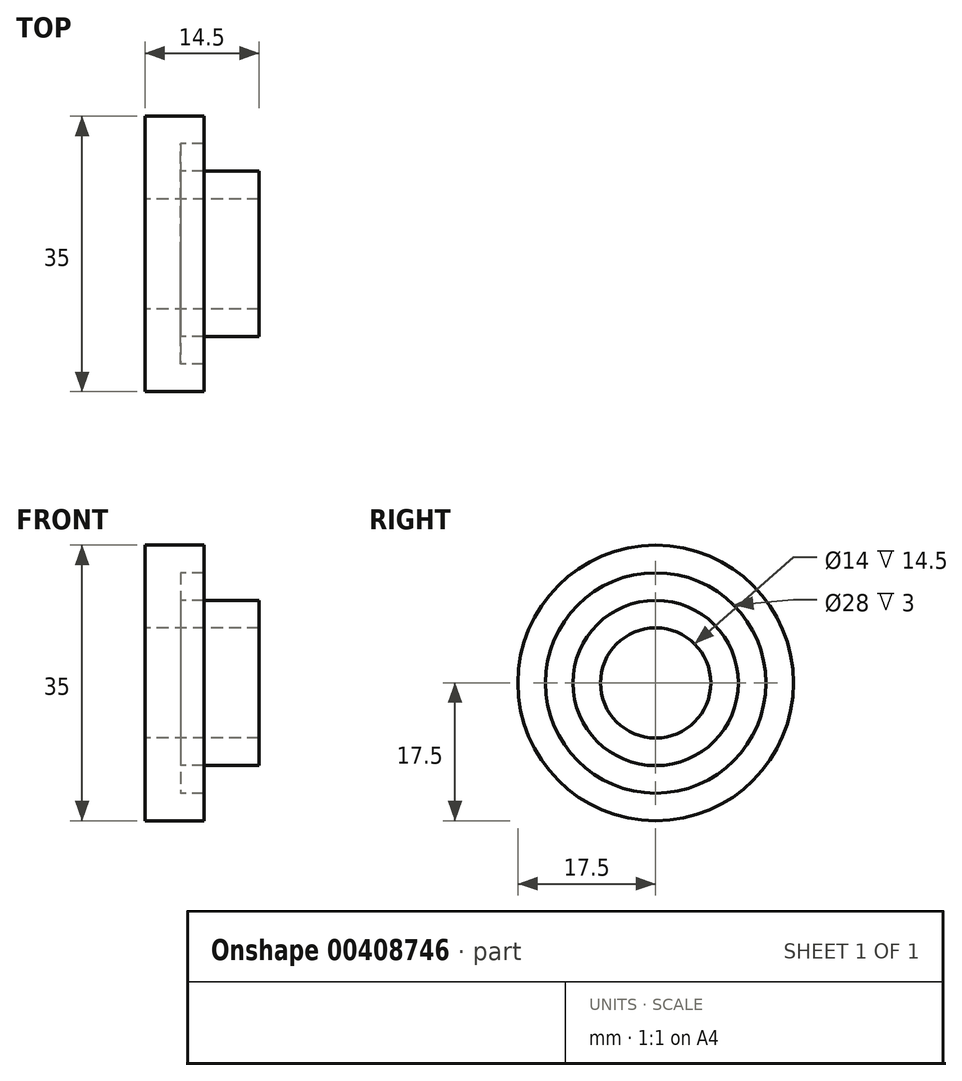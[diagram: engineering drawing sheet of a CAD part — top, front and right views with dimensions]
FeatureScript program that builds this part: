
annotation { "Feature Type Name" : "Feature", "Feature Type Description" : "" }
export const myFeature = defineFeature(function(context is Context, id is Id, definition is map)
    precondition{}
    {
        {
            var Q0;
            Q0=qCreatedBy(makeId("Front.planeOp"),FACE);
            var sketch = newSketch(context, id + "F0", { "sketchPlane" : qUnion([Q0])});
            skLineSegment(sketch, "E0", {"start": v(14.5, 7) * mm, "end": v(0, 7) * mm});
            skLineSegment(sketch, "E1", {"start": v(0, 7) * mm, "end": v(0, 17.5) * mm});
            skLineSegment(sketch, "E2", {"start": v(0, 17.5) * mm, "end": v(7.5, 17.5) * mm});
            skLineSegment(sketch, "E3", {"start": v(7.5, 17.5) * mm, "end": v(7.5, 14) * mm});
            skLineSegment(sketch, "E4", {"start": v(7.5, 14) * mm, "end": v(4.5, 14) * mm});
            skLineSegment(sketch, "E5", {"start": v(4.5, 14) * mm, "end": v(4.5, 10.5) * mm});
            skLineSegment(sketch, "E6", {"start": v(4.5, 10.5) * mm, "end": v(14.5, 10.5) * mm});
            skLineSegment(sketch, "E7", {"start": v(14.5, 10.5) * mm, "end": v(14.5, 7) * mm});
            skLineSegment(sketch, "E8", {"start": v(0, 0) * mm, "end": v(45.5, 0) * mm, "construction": true});
            skSolve(sketch);
        }
        {
            var Q0;
            Q0=makeQuery(id+"F0.imprint","IMPRINT",FACE,{"disambiguationData":[TD([[makeQuery(id+"F0.imprint","IMPRINT",EDGE,{"derivedFrom":sQuery(id+"F0.wireOp",EDGE,"E0")}),-1.0]])]});
            var Q1;
            Q1=sQuery(id+"F0.wireOp",EDGE,"E8");
            revolve(context, id + "F1", {"entities" : qUnion([Q0]), "axis" : qUnion([Q1]), "revolveType" : RevolveType.FULL});
        }
    });
